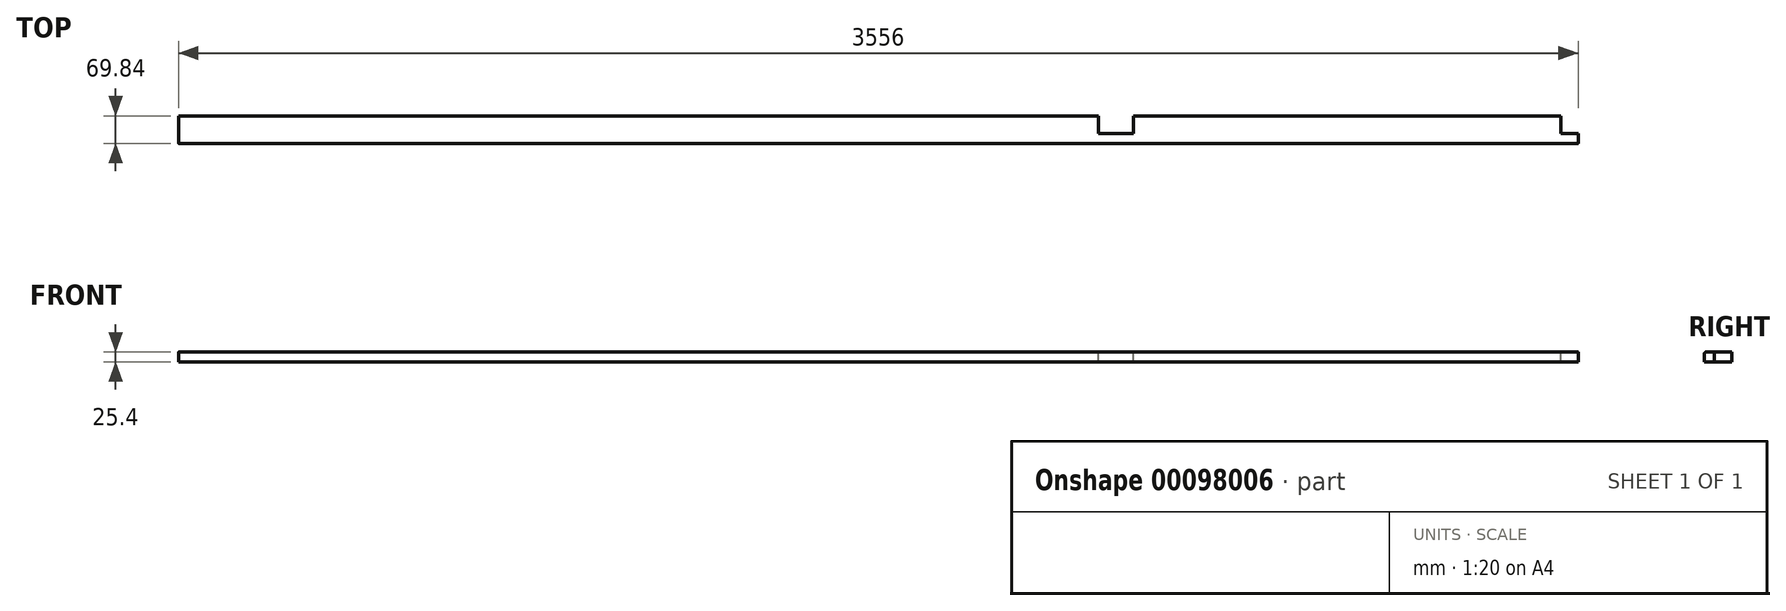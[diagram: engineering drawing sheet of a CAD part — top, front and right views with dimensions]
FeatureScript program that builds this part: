
annotation { "Feature Type Name" : "Feature", "Feature Type Description" : "" }
export const myFeature = defineFeature(function(context is Context, id is Id, definition is map)
    precondition{}
    {
        {
            var Q0;
            Q0=qCreatedBy(makeId("Top.planeOp"),FACE);
            var sketch = newSketch(context, id + "F0", { "sketchPlane" : qUnion([Q0])});
            skLineSegment(sketch, "E0.bottom", {"start": v(1778, 34.93) * mm, "end": v(-1778, 34.93) * mm});
            skLineSegment(sketch, "E0.top", {"start": v(1778, -34.93) * mm, "end": v(-1778, -34.93) * mm});
            skLineSegment(sketch, "E0.left", {"start": v(1778, 34.93) * mm, "end": v(1778, -34.93) * mm});
            skLineSegment(sketch, "E0.right", {"start": v(-1778, 34.93) * mm, "end": v(-1778, -34.93) * mm});
            skPoint(sketch, "E0.middle", {"position": v(0, 0) * mm});
            skSolve(sketch);
        }
        {
            var Q0;
            Q0=makeQuery(id+"F0.imprint","IMPRINT",FACE,{"disambiguationData":[TD([[makeQuery(id+"F0.imprint","IMPRINT",EDGE,{"derivedFrom":sQuery(id+"F0.wireOp",EDGE,"E0.bottom")}),1.0]])]});
            extrude(context, id + "F1", {"entities" : qUnion([Q0]), "depth" : 25.4 * mm});
        }
        {
            var Q0;
            Q0=makeQuery(id+"F1.opExtrude","CAP_FACE",FACE,{"disambiguationData":[OSD([sQuery(id+"F0.wireOp",EDGE,"E0.bottom"),sQuery(id+"F0.wireOp",EDGE,"E0.top"),sQuery(id+"F0.wireOp",EDGE,"E0.left"),sQuery(id+"F0.wireOp",EDGE,"E0.right")])],"isStart":false});
            var sketch = newSketch(context, id + "F2", { "sketchPlane" : qUnion([Q0])});
            skLineSegment(sketch, "E1", {"start": v(1778, 34.93) * mm, "end": v(1733.55, 34.93) * mm});
            skLineSegment(sketch, "E2", {"start": v(1733.55, 34.93) * mm, "end": v(1733.55, -9.52) * mm});
            skLineSegment(sketch, "E3", {"start": v(1733.55, -9.52) * mm, "end": v(1778, -9.52) * mm});
            skLineSegment(sketch, "E4", {"start": v(1778, -9.52) * mm, "end": v(1778, 34.93) * mm});
            skSolve(sketch);
        }
        {
            var Q0;
            Q0 = qSketchRegion(id + "F2", true);
            extrude(context, id + "F3", {"entities" : qUnion([Q0]), "operationType" : NewBodyOperationType.REMOVE, "endBound" : BoundingType.THROUGH_ALL, "oppositeDirection" : true, "depth" : 25.4 * mm});
        }
        {
            var Q0;
            Q0=makeQuery(id+"F1.opExtrude","CAP_FACE",FACE,{"disambiguationData":[OSD([sQuery(id+"F0.wireOp",EDGE,"E0.bottom"),sQuery(id+"F0.wireOp",EDGE,"E0.top"),sQuery(id+"F0.wireOp",EDGE,"E0.left"),sQuery(id+"F0.wireOp",EDGE,"E0.right")])],"isStart":false});
            var sketch = newSketch(context, id + "F4", { "sketchPlane" : qUnion([Q0])});
            skLineSegment(sketch, "E5", {"start": v(647.7, 34.93) * mm, "end": v(647.7, -9.52) * mm});
            skLineSegment(sketch, "E6", {"start": v(647.7, -9.52) * mm, "end": v(558.8, -9.52) * mm});
            skLineSegment(sketch, "E7", {"start": v(558.8, -9.52) * mm, "end": v(558.8, 34.93) * mm});
            skLineSegment(sketch, "E8", {"start": v(558.8, 34.93) * mm, "end": v(647.7, 34.93) * mm});
            skSolve(sketch);
        }
        {
            var Q0;
            Q0 = qSketchRegion(id + "F4", true);
            extrude(context, id + "F5", {"entities" : qUnion([Q0]), "operationType" : NewBodyOperationType.REMOVE, "endBound" : BoundingType.THROUGH_ALL, "oppositeDirection" : true, "depth" : 25.4 * mm});
        }
        {
            var Q0;
            Q0=makeQuery(id+"F1.opExtrude","CAP_EDGE",EDGE,{"disambiguationData":[OSD([sQuery(id+"F0.wireOp",EDGE,"E0.top")])],"isStart":false});
            fillet(context, id + "F6", {"entities" : qUnion([Q0]), "radius" : 5.08 * mm, "tangentPropagation" : true, "allowEdgeOverflow" : false});
        }
    });
